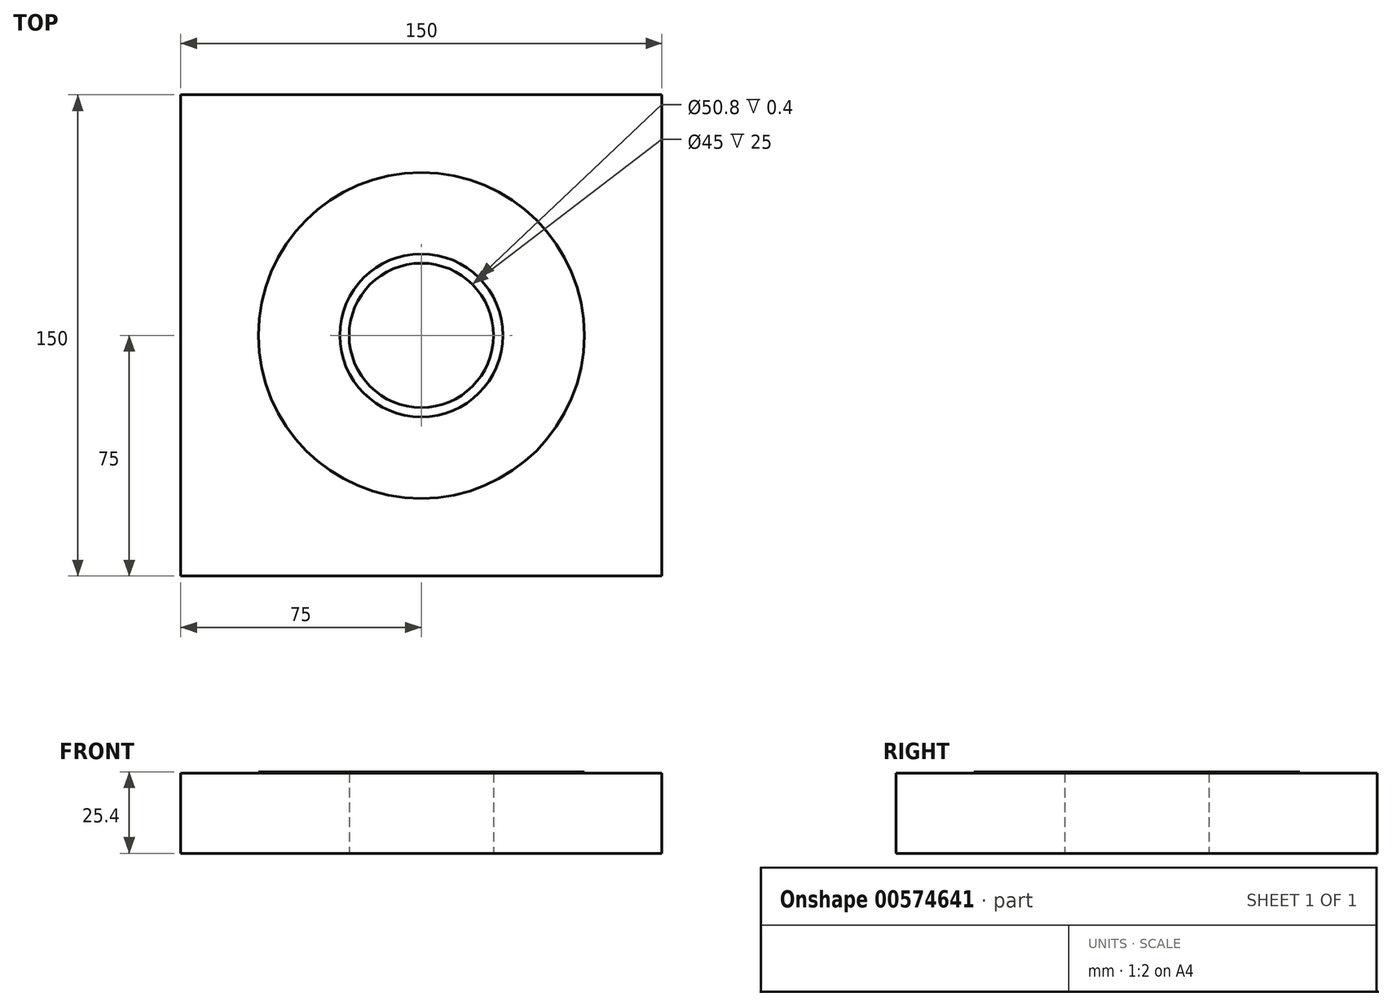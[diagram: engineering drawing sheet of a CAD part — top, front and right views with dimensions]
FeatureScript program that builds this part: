
annotation { "Feature Type Name" : "Feature", "Feature Type Description" : "" }
export const myFeature = defineFeature(function(context is Context, id is Id, definition is map)
    precondition{}
    {
        {
            var Q0;
            Q0=qCreatedBy(makeId("Top.planeOp"),FACE);
            var sketch = newSketch(context, id + "F0", { "sketchPlane" : qUnion([Q0])});
            skCircle(sketch, "E0", {"center": v(0, 0) * mm, "radius": 25.4 * mm});
            skCircle(sketch, "E1", {"center": v(0, 0) * mm, "radius": 50.8 * mm});
            skSolve(sketch);
        }
        {
            var Q0;
            Q0 = qSketchRegion(id + "F0", true);
            extrude(context, id + "F1", {"entities" : qUnion([Q0]), "depth" : 25.4 * mm, "offsetDistance" : 25.4 * mm});
        }
        {
            var Q0;
            Q0=qCreatedBy(makeId("Top.planeOp"),FACE);
            var sketch = newSketch(context, id + "F2", { "sketchPlane" : qUnion([Q0])});
            skLineSegment(sketch, "E2.bottom", {"start": v(75, 75) * mm, "end": v(-75, 75) * mm});
            skLineSegment(sketch, "E2.top", {"start": v(75, -75) * mm, "end": v(-75, -75) * mm});
            skLineSegment(sketch, "E2.left", {"start": v(75, 75) * mm, "end": v(75, -75) * mm});
            skLineSegment(sketch, "E2.right", {"start": v(-75, 75) * mm, "end": v(-75, -75) * mm});
            skPoint(sketch, "E2.middle", {"position": v(0, 0) * mm});
            skCircle(sketch, "E3.0", {"center": v(0, 0) * mm, "radius": 25.4 * mm});
            skCircle(sketch, "E4.0", {"center": v(0, 0) * mm, "radius": 50.8 * mm});
            skSolve(sketch);
        }
        {
            var Q0;
            Q0 = qSketchRegion(id + "F2", true);
            extrude(context, id + "F3", {"entities" : qUnion([Q0]), "operationType" : NewBodyOperationType.ADD, "depth" : 25 * mm, "offsetDistance" : 25 * mm});
        }
        {
            var Q0;
            Q0=qCreatedBy(makeId("Top.planeOp"),FACE);
            var sketch = newSketch(context, id + "F4", { "sketchPlane" : qUnion([Q0])});
            skCircle(sketch, "E5.0", {"center": v(0, 0) * mm, "radius": 25.4 * mm});
            skCircle(sketch, "E6", {"center": v(0, 0) * mm, "radius": 22.5 * mm});
            skSolve(sketch);
        }
        {
            var Q0;
            Q0 = qSketchRegion(id + "F4", true);
            extrude(context, id + "F5", {"entities" : qUnion([Q0]), "operationType" : NewBodyOperationType.ADD, "depth" : 25 * mm, "offsetDistance" : 25 * mm});
        }
        {
            var Q0;
            Q0=qCreatedBy(makeId("Top.planeOp"),FACE);
            var sketch = newSketch(context, id + "F6", { "sketchPlane" : qUnion([Q0])});
            skLineSegment(sketch, "E7.0.0", {"start": v(-75, -75) * mm, "end": v(75, -75) * mm, "construction": true});
            skLineSegment(sketch, "E7.0.1", {"start": v(75, -75) * mm, "end": v(75, 75) * mm});
            skLineSegment(sketch, "E7.0.2", {"start": v(75, 75) * mm, "end": v(-75, 75) * mm, "construction": true});
            skLineSegment(sketch, "E8.bottom", {"start": v(75, -75) * mm, "end": v(50, -75) * mm});
            skLineSegment(sketch, "E8.top", {"start": v(75, 75) * mm, "end": v(50, 75) * mm});
            skLineSegment(sketch, "E8.right", {"start": v(50, -75) * mm, "end": v(50, 75) * mm});
            skLineSegment(sketch, "E9.bottom", {"start": v(-75, 75) * mm, "end": v(-75, 75) * mm});
            skLineSegment(sketch, "E9.top", {"start": v(-75, -75) * mm, "end": v(-75, -75) * mm});
            skSolve(sketch);
        }
        {
            var Q0;
            Q0 = qConstructionFilter(qBodyType(qCreatedBy(id + "F6" ,EDGE), BodyType.WIRE), ConstructionObject.NO);
            extrude(context, id + "F7", {"bodyType" : ToolBodyType.SURFACE, "surfaceEntities" : qUnion([Q0]), "oppositeDirection" : true, "depth" : 83 * mm, "offsetDistance" : 25 * mm});
        }
    });
